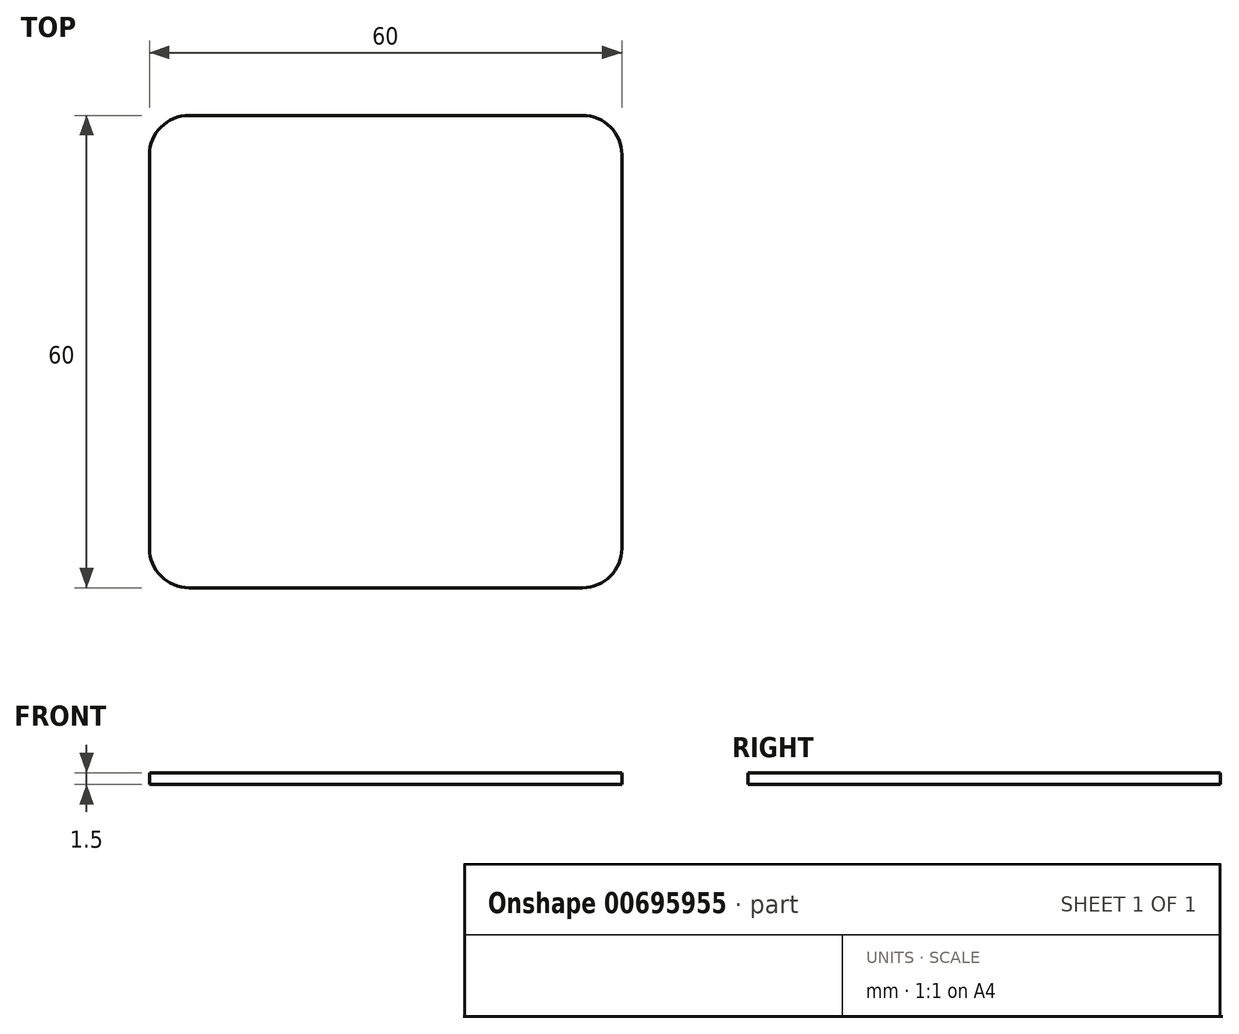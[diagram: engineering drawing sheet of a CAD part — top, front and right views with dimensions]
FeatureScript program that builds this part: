
annotation { "Feature Type Name" : "Feature", "Feature Type Description" : "" }
export const myFeature = defineFeature(function(context is Context, id is Id, definition is map)
    precondition{}
    {
        {
            var Q0;
            Q0=qCreatedBy(makeId("Top.planeOp"),FACE);
            var sketch = newSketch(context, id + "F0", { "sketchPlane" : qUnion([Q0])});
            skLineSegment(sketch, "E0.bottom", {"start": v(-25, 30) * mm, "end": v(25, 30) * mm});
            skLineSegment(sketch, "E0.top", {"start": v(-25, -30) * mm, "end": v(25, -30) * mm});
            skLineSegment(sketch, "E0.left", {"start": v(-30, 25) * mm, "end": v(-30, -25) * mm});
            skLineSegment(sketch, "E0.right", {"start": v(30, 25) * mm, "end": v(30, -25) * mm});
            skPoint(sketch, "E0.middle", {"position": v(0, 0) * mm});
            skPoint(sketch, "E1.visualSharp", {"position": v(-30, 30) * mm});
            skArc(sketch, "E1.filletArc", {"start": v(-25, 30) * mm, "mid": v(-28.54, 28.54) * mm, "end": v(-30, 25) * mm});
            skPoint(sketch, "E2.visualSharp", {"position": v(30, 30) * mm});
            skArc(sketch, "E2.filletArc", {"start": v(30, 25) * mm, "mid": v(28.54, 28.54) * mm, "end": v(25, 30) * mm});
            skPoint(sketch, "E3.visualSharp", {"position": v(30, -30) * mm});
            skArc(sketch, "E3.filletArc", {"start": v(25, -30) * mm, "mid": v(28.54, -28.54) * mm, "end": v(30, -25) * mm});
            skPoint(sketch, "E4.visualSharp", {"position": v(-30, -30) * mm});
            skArc(sketch, "E4.filletArc", {"start": v(-30, -25) * mm, "mid": v(-28.54, -28.54) * mm, "end": v(-25, -30) * mm});
            skSolve(sketch);
        }
        {
            var Q0;
            Q0=makeQuery(id+"F0.imprint","IMPRINT",FACE,{"disambiguationData":[TD([[makeQuery(id+"F0.imprint","IMPRINT",EDGE,{"derivedFrom":sQuery(id+"F0.wireOp",EDGE,"E0.bottom")}),-1.0]])]});
            extrude(context, id + "F1", {"entities" : qUnion([Q0]), "depth" : 1.5 * mm, "offsetDistance" : 25 * mm});
        }
    });
